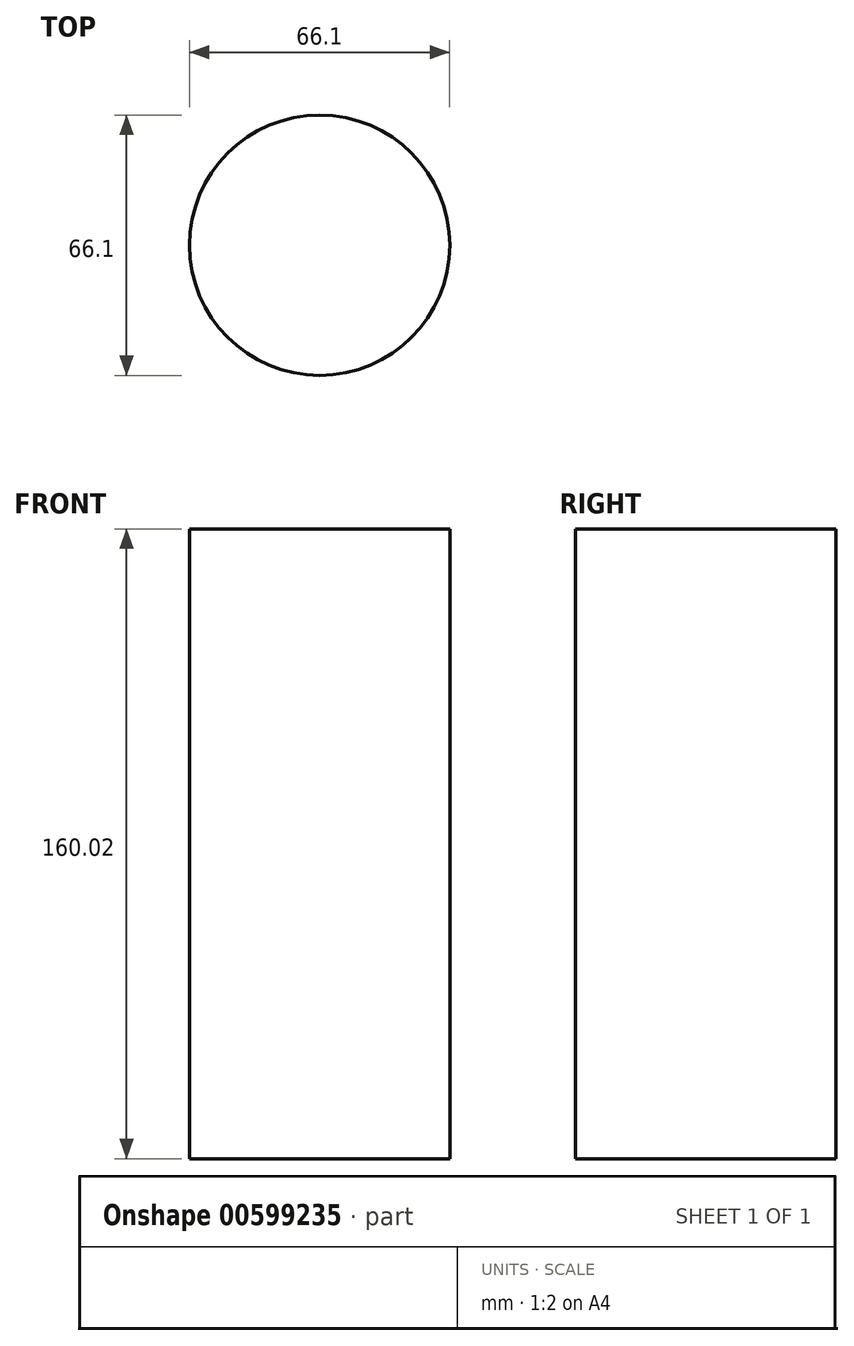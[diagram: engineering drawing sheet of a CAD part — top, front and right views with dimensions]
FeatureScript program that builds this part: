
annotation { "Feature Type Name" : "Feature", "Feature Type Description" : "" }
export const myFeature = defineFeature(function(context is Context, id is Id, definition is map)
    precondition{}
    {
        {
            var Q0;
            Q0=qCreatedBy(makeId("Top.planeOp"),FACE);
            var sketch = newSketch(context, id + "F0", { "sketchPlane" : qUnion([Q0])});
            skCircle(sketch, "E0", {"center": v(0, 0) * mm, "radius": 33.05 * mm});
            skSolve(sketch);
        }
        {
            var Q0;
            Q0 = qSketchRegion(id + "F0", true);
            extrude(context, id + "F1", {"entities" : qUnion([Q0]), "depth" : 160.02 * mm, "offsetDistance" : 25.4 * mm});
        }
    });
